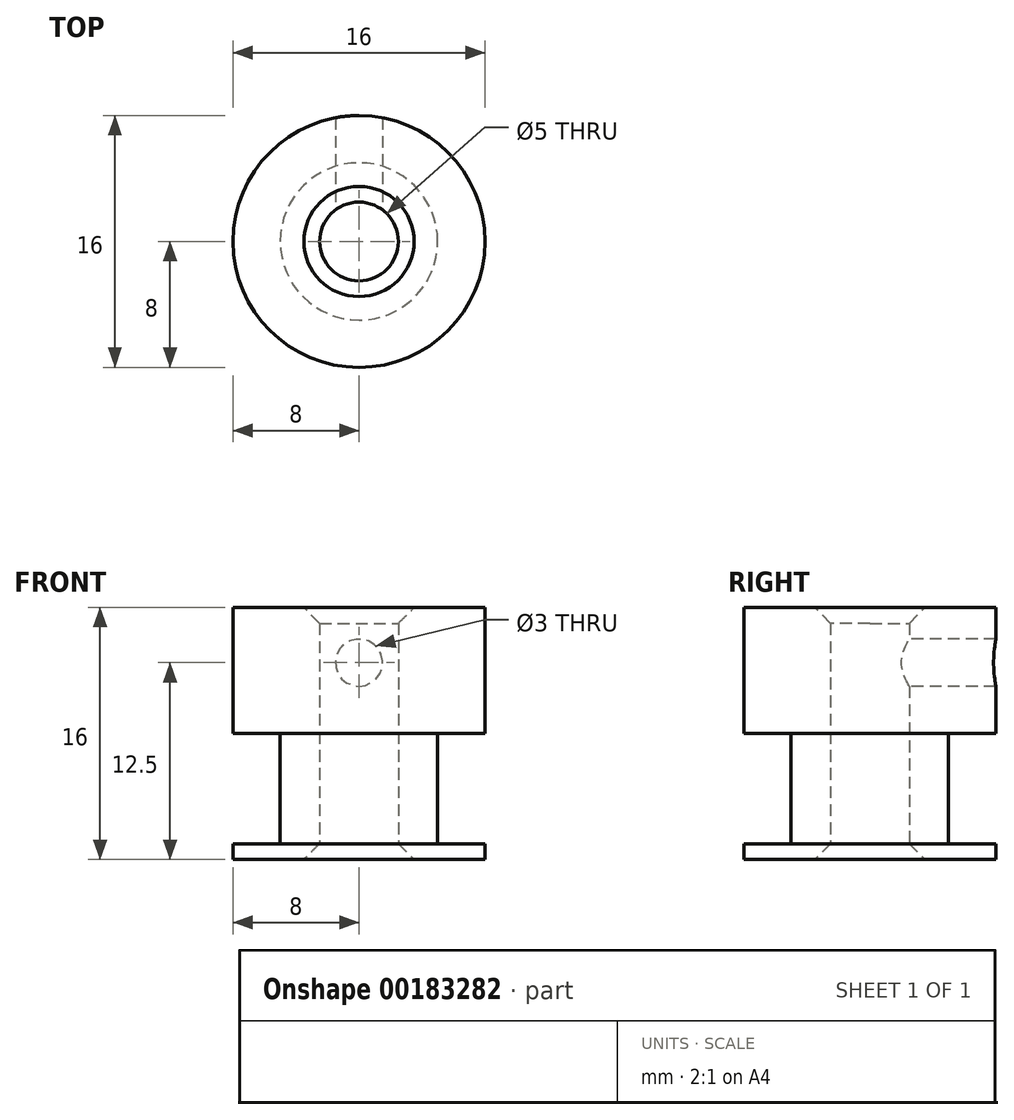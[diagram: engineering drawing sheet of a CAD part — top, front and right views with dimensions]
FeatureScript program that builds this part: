
annotation { "Feature Type Name" : "Feature", "Feature Type Description" : "" }
export const myFeature = defineFeature(function(context is Context, id is Id, definition is map)
    precondition{}
    {
        {
            var Q0;
            Q0=qCreatedBy(makeId("Top.planeOp"),FACE);
            var sketch = newSketch(context, id + "F0", { "sketchPlane" : qUnion([Q0])});
            skCircle(sketch, "E0", {"center": v(0, 0) * mm, "radius": 2.5 * mm});
            skCircle(sketch, "E1", {"center": v(0, 0) * mm, "radius": 5 * mm});
            skSolve(sketch);
        }
        {
            var Q0;
            Q0=qSketchRegion(id+"F0",true);
            extrude(context, id + "F1", {"entities" : qUnion([Q0]), "endBound" : BoundingType.SYMMETRIC, "depth" : 7 * mm});
        }
        {
            var Q0;
            Q0=makeQuery(id+"F1.opExtrude","CAP_FACE",FACE,{"disambiguationData":[OSD([sQuery(id+"F0.wireOp",EDGE,"E0"),sQuery(id+"F0.wireOp",EDGE,"E1")])],"isStart":false});
            var sketch = newSketch(context, id + "F2", { "sketchPlane" : qUnion([Q0])});
            skCircle(sketch, "E2", {"center": v(0, 0) * mm, "radius": 8 * mm});
            skCircle(sketch, "E3.0", {"center": v(0, 0) * mm, "radius": 2.5 * mm});
            skSolve(sketch);
        }
        {
            var Q0;
            Q0=qSketchRegion(id+"F2",true);
            extrude(context, id + "F3", {"entities" : qUnion([Q0]), "depth" : 1 * mm});
        }
        {
            var Q0;
            Q0=makeQuery(id+"F3.opExtrude","SWEPT_BODY",BODY,{"disambiguationData":[OSD([sQuery(id+"F2.wireOp",EDGE,"E2"),sQuery(id+"F2.wireOp",EDGE,"E3.0")])]});
            var Q1;
            Q1=qCreatedBy(makeId("Top.planeOp"),FACE);
            mirror(context, id + "F4", {"operationType" : NewBodyOperationType.ADD, "entities" : qUnion([Q0]), "mirrorPlane" : qUnion([Q1])});
        }
        {
            var Q0;
            Q0=makeQuery(id+"F3.opExtrude","CAP_FACE",FACE,{"disambiguationData":[OSD([sQuery(id+"F2.wireOp",EDGE,"E2"),sQuery(id+"F2.wireOp",EDGE,"E3.0")])],"isStart":false});
            var sketch = newSketch(context, id + "F5", { "sketchPlane" : qUnion([Q0])});
            skCircle(sketch, "E4.0", {"center": v(0, 0) * mm, "radius": 2.5 * mm});
            skCircle(sketch, "E5.0", {"center": v(0, 0) * mm, "radius": 8 * mm});
            skSolve(sketch);
        }
        {
            var Q0;
            Q0=qSketchRegion(id+"F5",true);
            extrude(context, id + "F6", {"entities" : qUnion([Q0]), "operationType" : NewBodyOperationType.ADD, "depth" : 7 * mm});
        }
        {
            var Q0;
            Q0=makeQuery(id+"F6.opExtrude","CAP_EDGE",EDGE,{"disambiguationData":[OSD([sQuery(id+"F5.wireOp",EDGE,"Srn6Zubq-rTGP-wvjp-bq31-RlFgEQHIz4FP")])],"isStart":false});
            var Q1;
            Q1=makeQuery(id+"F6.opExtrude","CAP_EDGE",EDGE,{"disambiguationData":[OSD([sQuery(id+"F5.wireOp",EDGE,"E4.0")])],"isStart":false});
            var Q2;
            Q2=makeQuery(id+"F4.opPattern","COPY",EDGE,{"derivedFrom":makeQuery(id+"F3.opExtrude","CAP_EDGE",EDGE,{"disambiguationData":[OSD([sQuery(id+"F2.wireOp",EDGE,"E3.0")])],"isStart":false}),"instanceName":"1"});
            chamfer(context, id + "F7", {"entities" : qUnion([Q0, Q1, Q2]), "width" : 1 * mm, "tangentPropagation" : true});
        }
        {
            var Q0;
            Q0=qCreatedBy(makeId("Front.planeOp"),FACE);
            var sketch = newSketch(context, id + "F8", { "sketchPlane" : qUnion([Q0])});
            skCircle(sketch, "E6", {"center": v(0, 8) * mm, "radius": 1.5 * mm});
            skLineSegment(sketch, "E7", {"start": v(0, 11.5) * mm, "end": v(0, 4.5) * mm, "construction": true});
            skSolve(sketch);
        }
        {
            var Q0;
            Q0=qSketchRegion(id+"F8",true);
            extrude(context, id + "F9", {"entities" : qUnion([Q0]), "operationType" : NewBodyOperationType.REMOVE, "endBound" : BoundingType.THROUGH_ALL, "oppositeDirection" : true, "depth" : 25 * mm});
        }
    });
